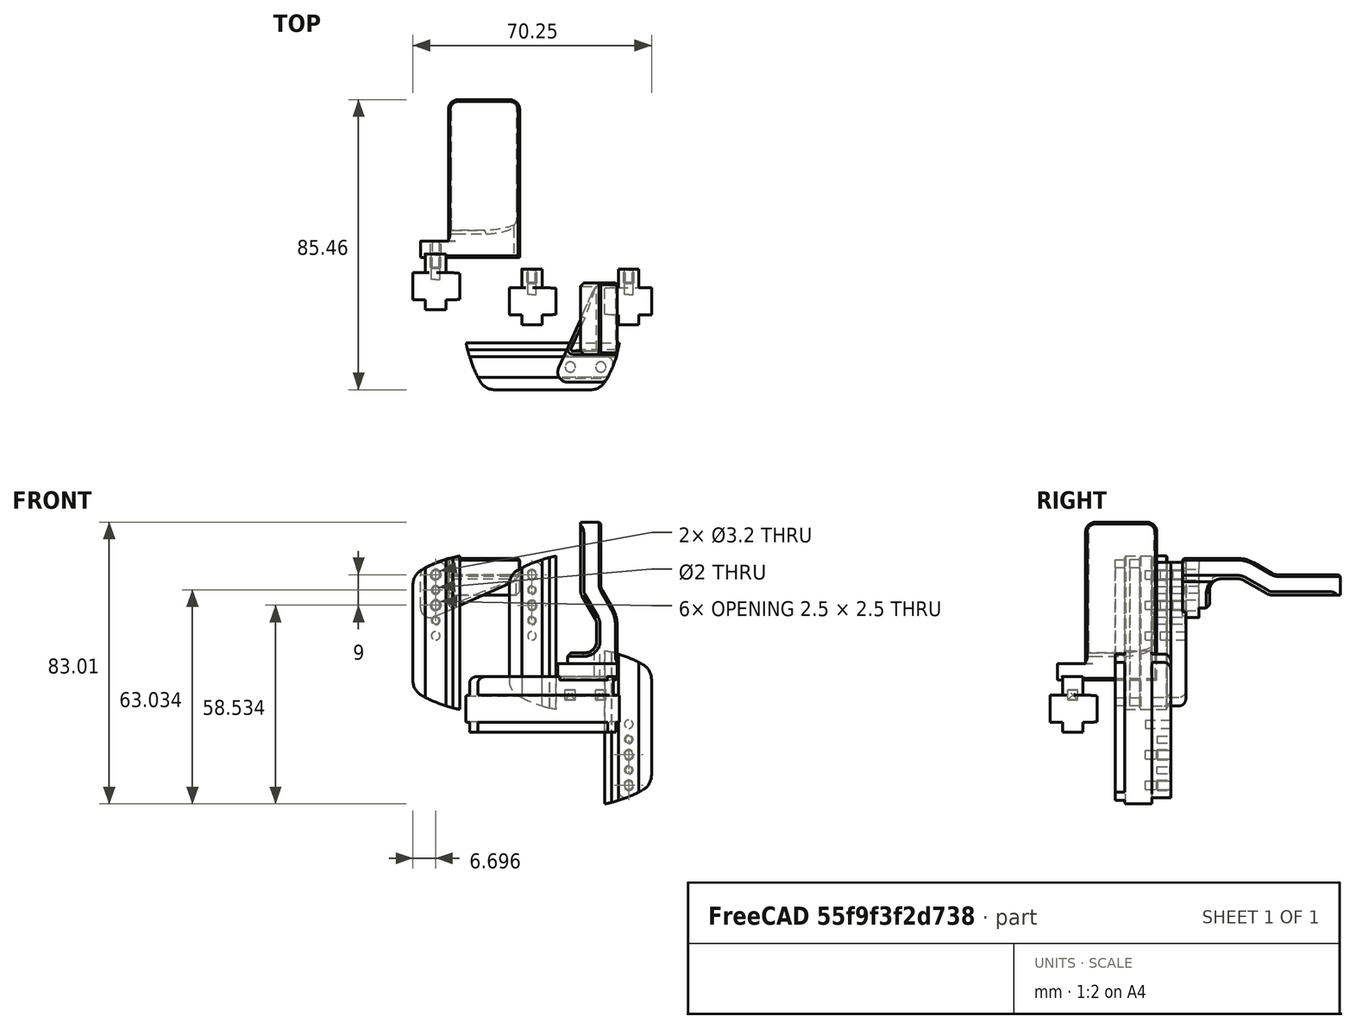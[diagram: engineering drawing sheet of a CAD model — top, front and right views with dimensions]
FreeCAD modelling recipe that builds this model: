
FCSTD DOCUMENT  (FreeCAD 1.0R39109 (Git))
Label: finger
objects: Part::Feature×4, App::Part×1, Part::Plane×1, Part::FeaturePython×1, Part::Box×1, Part::Cut×1
note: 8 computed .brp shape members not serialized (recipe doc carries the construction recipe); baked Part::Feature solids carry a one-line shape summary decoded from their .brp

FEATURE [Part::Feature] Part__Feature008  label="D-A03-ASM_DOIGTS_PARALLELES-1^ROBOTIQ_HAND-E_DEFEATURE_NO_FINGERTIPS"
FEATURE [App::Part] ROBOTIQ_HAND_E_DEFEATURE_NO_FINGERTIPS  label="ROBOTIQ_HAND-E_DEFEATURE_NO_FINGERTIPS"
  Group = -> [Part__Feature008]
  Origin = -> Origin
  Placement = pos=(0,0,0) rot=(0.57735,0.57735,0.57735;2.0944rad)
FEATURE [Part::Plane] Plane
  AttacherType = Attacher::AttachEngine3D
  Length = 10
  Placement = pos=(0,0,0) rot=(0,1,0;1.5708rad)
  Width = 10
FEATURE [Part::FeaturePython] Slice  # WARN: FeaturePython — macro-defined, semantics opaque (R4)
  Base = -> Part__Feature008
  Mode = 1
  Tolerance = 0
  Tools = -> [Plane]
FEATURE [Part::Box] Box  label="Cube"
  AttacherType = Attacher::AttachEngine3D
  Height = 60
  Length = 20
  Placement = pos=(4,-3,-38) rot=(0,0,1;0rad)
  Width = 20
FEATURE [Part::Cut] Cut
  Base = -> Part__Feature008
  Placement = pos=(-28.3544,4.43246,0.0101298) rot=(0,0,1;0rad)
  Tool = -> Box
FEATURE [Part::Feature] Part__Feature  label="D-018-DOIGT_DȃALǀ"
  Placement = pos=(-28.3644,64.5325,19.0241) rot=(0,0,-1;1.5708rad)
FEATURE [Part::Feature] Defeatured
  Placement = pos=(-25,28.37,-18.03) rot=(0.57735,0.57735,0.57735;2.0944rad)
FEATURE [Part::Feature] Defeatured001
  Placement = pos=(-25,28.37,-18.03) rot=(0.57735,0.57735,0.57735;2.0944rad)
